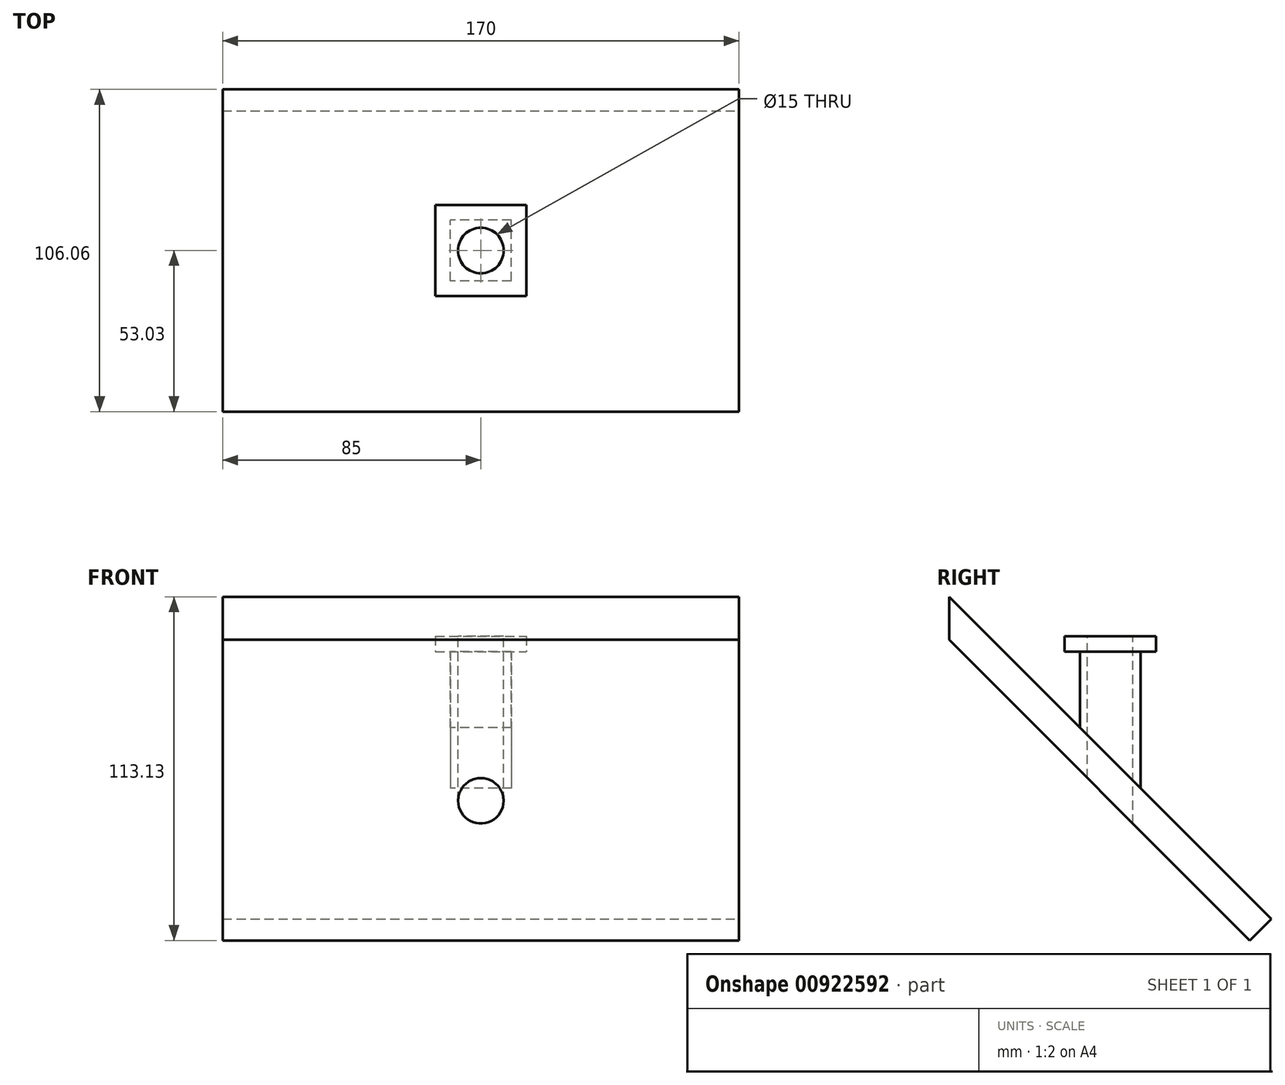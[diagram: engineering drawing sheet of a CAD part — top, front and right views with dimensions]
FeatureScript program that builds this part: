
annotation { "Feature Type Name" : "Feature", "Feature Type Description" : "" }
export const myFeature = defineFeature(function(context is Context, id is Id, definition is map)
    precondition{}
    {
        {
            var Q0;
            Q0=qCreatedBy(makeId("Front.planeOp"),FACE);
            var Q1;
            Q1=qCreatedBy(makeId("Top.planeOp"),FACE);
            cPlane(context, id + "F0", {"entities" : qUnion([Q0, Q1]), "cplaneType" : CPlaneType.MID_PLANE, "offset" : 25.4 * mm, "width" : 152.4 * mm, "height" : 152.4 * mm});
        }
        {
            var Q0;
            Q0=qCreatedBy(id+"F0.planeOp",FACE);
            var sketch = newSketch(context, id + "F1", { "sketchPlane" : qUnion([Q0])});
            skLineSegment(sketch, "E0.bottom", {"start": v(-85, 75) * mm, "end": v(85, 75) * mm});
            skLineSegment(sketch, "E0.top", {"start": v(-85, -75) * mm, "end": v(85, -75) * mm});
            skLineSegment(sketch, "E0.left", {"start": v(-85, 75) * mm, "end": v(-85, -75) * mm});
            skLineSegment(sketch, "E0.right", {"start": v(85, 75) * mm, "end": v(85, -75) * mm});
            skPoint(sketch, "E0.middle", {"position": v(0, 0) * mm});
            skSolve(sketch);
        }
        {
            var Q0;
            Q0 = qSketchRegion(id + "F1", true);
            extrude(context, id + "F2", {"entities" : qUnion([Q0]), "depth" : 10 * mm, "offsetDistance" : 25.4 * mm});
        }
        {
            var Q0;
            Q0=makeQuery(id+"F2.opExtrude","CAP_EDGE",EDGE,{"disambiguationData":[OSD([sQuery(id+"F1.wireOp",EDGE,"E0.bottom")])],"isStart":false});
            chamfer(context, id + "F3", {"entities" : qUnion([Q0]), "width" : 10 * mm, "tangentPropagation" : true});
        }
        {
            var Q0;
            Q0=qCreatedBy(makeId("Right.planeOp"),FACE);
            var sketch = newSketch(context, id + "F4", { "sketchPlane" : qUnion([Q0])});
            skLineSegment(sketch, "E1", {"start": v(-10, 10) * mm, "end": v(-10, 35) * mm});
            skLineSegment(sketch, "E2", {"start": v(-10, 35) * mm, "end": v(10, 35) * mm});
            skLineSegment(sketch, "E3", {"start": v(10, 35) * mm, "end": v(10, -10) * mm});
            skLineSegment(sketch, "E4.0", {"start": v(-53.03, 53.03) * mm, "end": v(53.03, -53.03) * mm, "construction": true});
            skLineSegment(sketch, "E5", {"start": v(-10, 10) * mm, "end": v(10, -10) * mm});
            skLineSegment(sketch, "E6", {"start": v(0, 0) * mm, "end": v(0, 35) * mm, "construction": true});
            skSolve(sketch);
        }
        {
            var Q0;
            Q0 = qSketchRegion(id + "F4", true);
            extrude(context, id + "F5", {"entities" : qUnion([Q0]), "operationType" : NewBodyOperationType.ADD, "depth" : 20 * mm, "offsetDistance" : 25.4 * mm, "symmetric" : true});
        }
        {
            var Q0;
            Q0=makeQuery(id+"F5.opExtrude","SWEPT_FACE",FACE,{"disambiguationData":[OSD([sQuery(id+"F4.wireOp",EDGE,"E2")])]});
            var sketch = newSketch(context, id + "F6", { "sketchPlane" : qUnion([Q0])});
            skLineSegment(sketch, "E7.bottom", {"start": v(-15, 15) * mm, "end": v(15, 15) * mm});
            skLineSegment(sketch, "E7.top", {"start": v(-15, -15) * mm, "end": v(15, -15) * mm});
            skLineSegment(sketch, "E7.left", {"start": v(-15, 15) * mm, "end": v(-15, -15) * mm});
            skLineSegment(sketch, "E7.right", {"start": v(15, 15) * mm, "end": v(15, -15) * mm});
            skPoint(sketch, "E7.middle", {"position": v(0, 0) * mm});
            skSolve(sketch);
        }
        {
            var Q0;
            Q0 = qSketchRegion(id + "F6", true);
            extrude(context, id + "F7", {"entities" : qUnion([Q0]), "operationType" : NewBodyOperationType.ADD, "depth" : 5 * mm, "offsetDistance" : 25.4 * mm});
        }
        {
            var Q0;
            Q0=makeQuery(id+"F7.opExtrude","CAP_FACE",FACE,{"disambiguationData":[OSD([sQuery(id+"F6.wireOp",EDGE,"E7.bottom"),sQuery(id+"F6.wireOp",EDGE,"E7.top"),sQuery(id+"F6.wireOp",EDGE,"E7.left"),sQuery(id+"F6.wireOp",EDGE,"E7.right")])],"isStart":false});
            var sketch = newSketch(context, id + "F8", { "sketchPlane" : qUnion([Q0])});
            skPoint(sketch, "E8.middle", {"position": v(0, 0) * mm});
            skCircle(sketch, "E9", {"center": v(0, 0) * mm, "radius": 7.5 * mm});
            skSolve(sketch);
        }
        {
            var Q0;
            Q0 = qSketchRegion(id + "F8", true);
            extrude(context, id + "F9", {"entities" : qUnion([Q0]), "operationType" : NewBodyOperationType.REMOVE, "endBound" : BoundingType.THROUGH_ALL, "oppositeDirection" : true, "depth" : 25.4 * mm, "offsetDistance" : 25.4 * mm});
        }
    });
